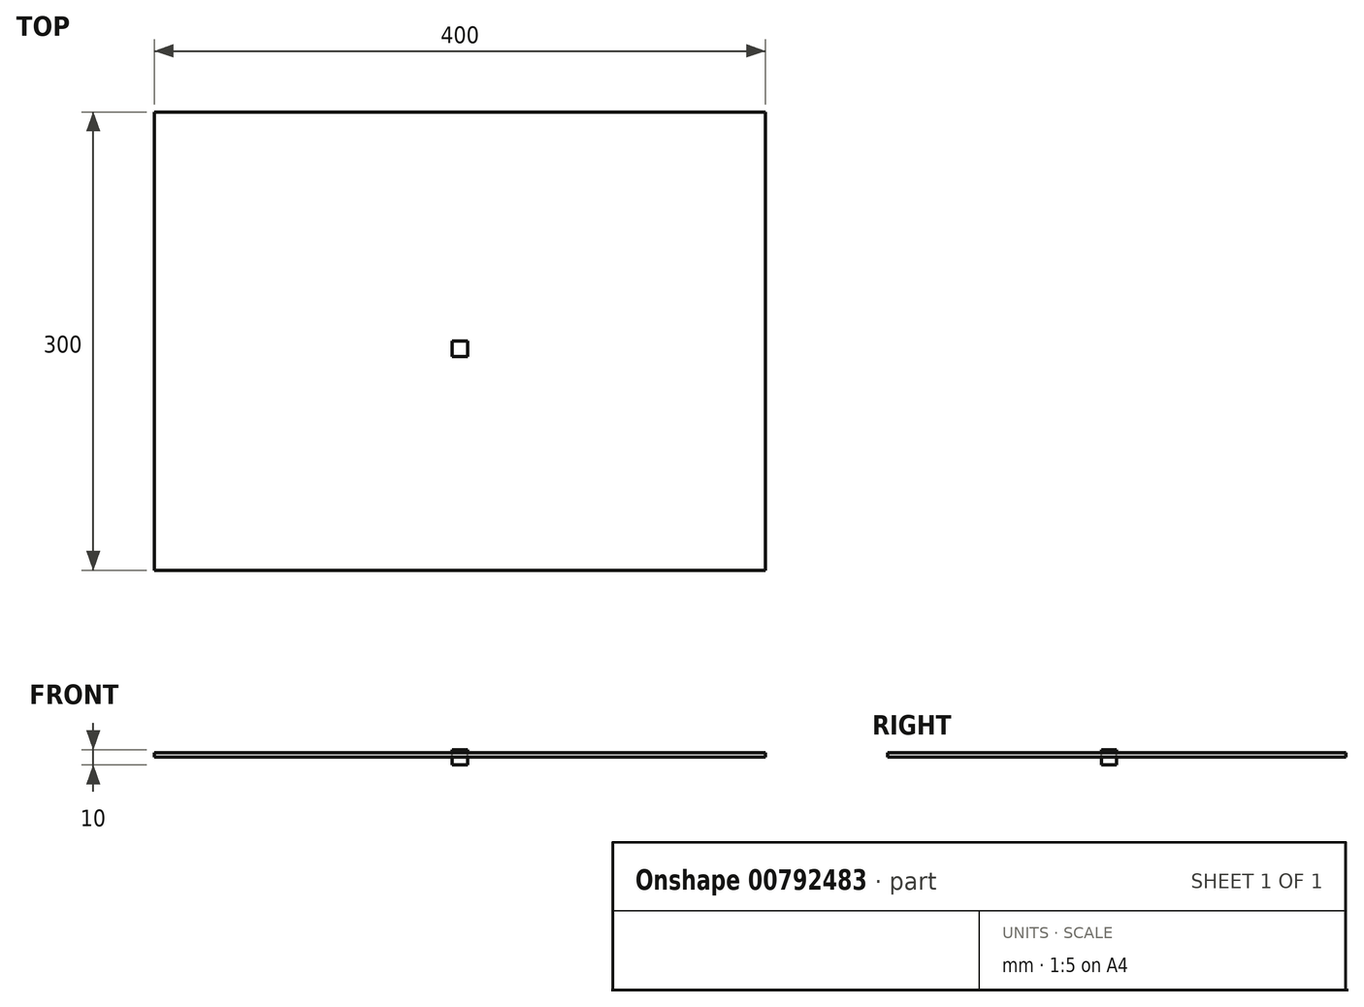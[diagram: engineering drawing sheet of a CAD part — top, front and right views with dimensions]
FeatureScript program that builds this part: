
annotation { "Feature Type Name" : "Feature", "Feature Type Description" : "" }
export const myFeature = defineFeature(function(context is Context, id is Id, definition is map)
    precondition{}
    {
        {
            var Q0;
            Q0=qCreatedBy(makeId("Top.planeOp"),FACE);
            var sketch = newSketch(context, id + "F0", { "sketchPlane" : qUnion([Q0])});
            skLineSegment(sketch, "E0.bottom", {"start": v(-200, 150) * mm, "end": v(200, 150) * mm});
            skLineSegment(sketch, "E0.top", {"start": v(-200, -150) * mm, "end": v(200, -150) * mm});
            skLineSegment(sketch, "E0.left", {"start": v(-200, 150) * mm, "end": v(-200, -150) * mm});
            skLineSegment(sketch, "E0.right", {"start": v(200, 150) * mm, "end": v(200, -150) * mm});
            skSolve(sketch);
        }
        {
            var Q0;
            Q0=makeQuery(id+"F0.imprint","IMPRINT",FACE,{"disambiguationData":[TD([[makeQuery(id+"F0.imprint","IMPRINT",EDGE,{"derivedFrom":sQuery(id+"F0.wireOp",EDGE,"E0.bottom")}),-1.0]])]});
            extrude(context, id + "F1", {"entities" : qUnion([Q0]), "depth" : 3 * mm, "offsetDistance" : 25 * mm});
        }
        {
            var Q0;
            Q0=qCreatedBy(makeId("Front.planeOp"),FACE);
            var sketch = newSketch(context, id + "F2", { "sketchPlane" : qUnion([Q0])});
            skLineSegment(sketch, "E1.bottom", {"start": v(5, -5) * mm, "end": v(-5, -5) * mm});
            skLineSegment(sketch, "E1.top", {"start": v(5, 5) * mm, "end": v(-5, 5) * mm});
            skLineSegment(sketch, "E1.left", {"start": v(5, -5) * mm, "end": v(5, 5) * mm});
            skLineSegment(sketch, "E1.right", {"start": v(-5, -5) * mm, "end": v(-5, 5) * mm});
            skPoint(sketch, "E1.middle", {"position": v(0, 0) * mm});
            skSolve(sketch);
        }
        {
            var Q0;
            Q0=makeQuery(id+"F2.imprint","IMPRINT",FACE,{"disambiguationData":[TD([[makeQuery(id+"F2.imprint","IMPRINT",EDGE,{"derivedFrom":sQuery(id+"F2.wireOp",EDGE,"E1.bottom")}),-1.0]])]});
            extrude(context, id + "F3", {"entities" : qUnion([Q0]), "depth" : 10 * mm, "offsetDistance" : 25 * mm});
        }
    });
